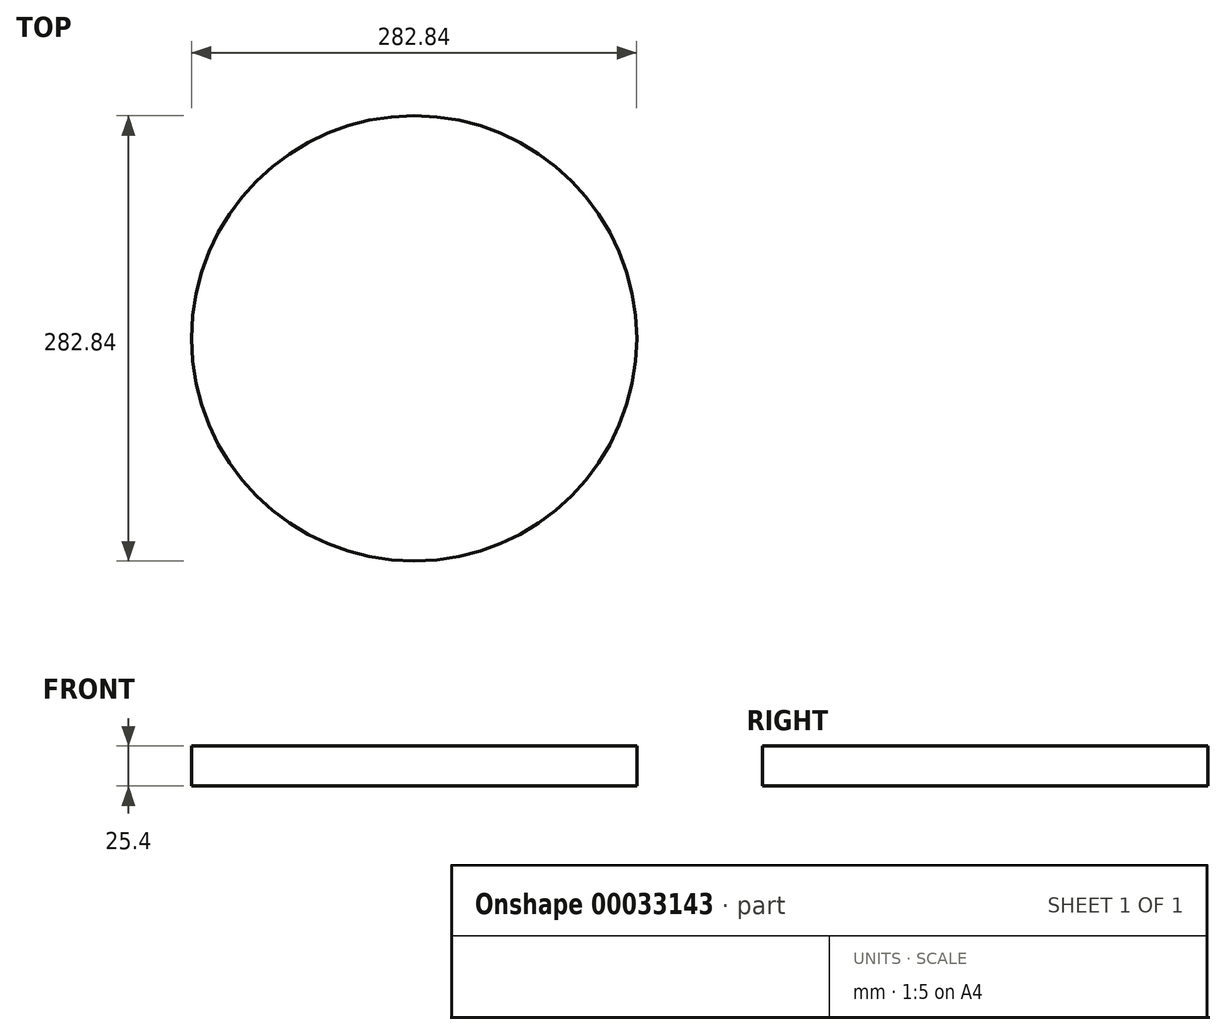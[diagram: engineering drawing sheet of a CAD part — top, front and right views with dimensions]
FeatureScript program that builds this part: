
annotation { "Feature Type Name" : "Feature", "Feature Type Description" : "" }
export const myFeature = defineFeature(function(context is Context, id is Id, definition is map)
    precondition{}
    {
        {
            var Q0;
            Q0=qCreatedBy(makeId("Top.planeOp"),FACE);
            var sketch = newSketch(context, id + "F0", { "sketchPlane" : qUnion([Q0])});
            skCircle(sketch, "E0", {"center": v(0, 0) * mm, "radius": 141.42 * mm});
            skSolve(sketch);
        }
        {
            var Q0;
            Q0 = qSketchRegion(id + "F0", true);
            extrude(context, id + "F1", {"entities" : qUnion([Q0]), "depth" : 25.4 * mm});
        }
    });
